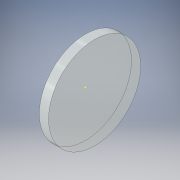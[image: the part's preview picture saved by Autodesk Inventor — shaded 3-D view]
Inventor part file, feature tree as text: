
AUTODESK INVENTOR PART (.ipt)
format: ipt  version: 2017 (Build 210142000, 142)  size: 106,496 bytes
history: native  units: in
note: dims shown in document units (in); Inventor stores cm internally (conversion verified against a paired STEP export)
features: sketch x2, extrude x1
ambient origin geometry x8: Origin, YZ Plane, XZ Plane, XY Plane, X Axis, Y Axis, Z Axis, Center Point
bodies: Solid1 (feature_tree)
feature tree (3):
  sketch  "Sketch1"  dims[d0=1.5748in d1=0.1575in d2=0.0in]
  extrude  "Extrusion1"  Depth=0.1575in TaperAngle=0.0deg
  sketch  "Sketch2"
